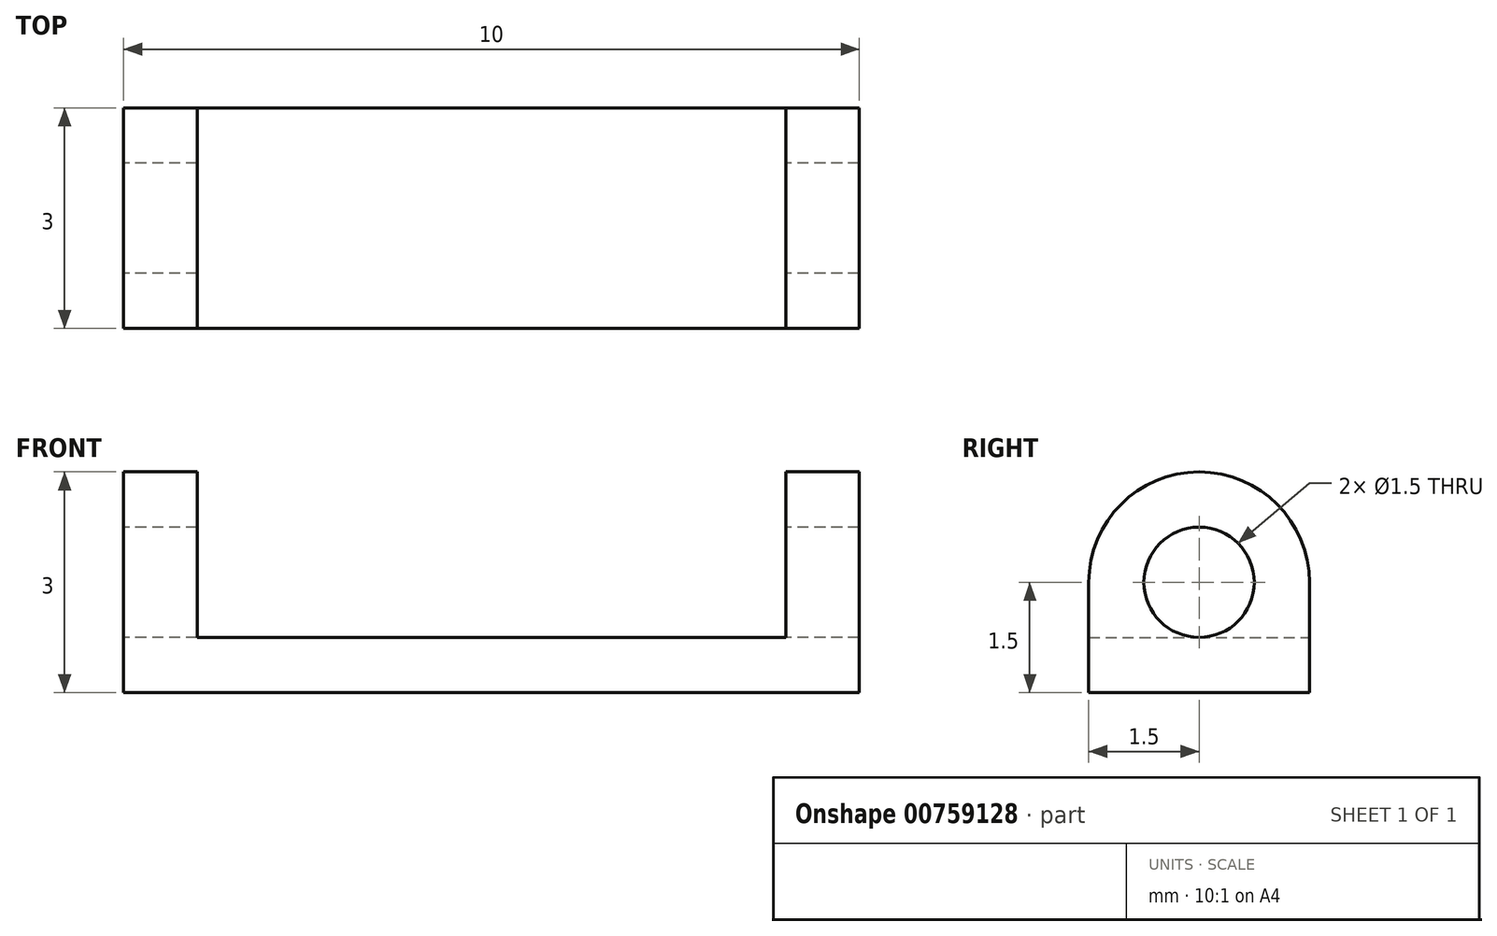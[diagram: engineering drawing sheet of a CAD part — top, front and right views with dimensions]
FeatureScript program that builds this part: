
annotation { "Feature Type Name" : "Feature", "Feature Type Description" : "" }
export const myFeature = defineFeature(function(context is Context, id is Id, definition is map)
    precondition{}
    {
        {
            assignVariable(context, id + "F0", {"name" : "b", "anyValue" : 3});
        }
        {
            var Q0;
            Q0=qCreatedBy(makeId("Top.planeOp"),FACE);
            var sketch = newSketch(context, id + "F1", { "sketchPlane" : qUnion([Q0])});
            skLineSegment(sketch, "E0.bottom", {"start": v(-5, 1.5) * mm, "end": v(5, 1.5) * mm});
            skLineSegment(sketch, "E0.top", {"start": v(-5, -1.5) * mm, "end": v(5, -1.5) * mm});
            skLineSegment(sketch, "E0.left", {"start": v(-5, 1.5) * mm, "end": v(-5, -1.5) * mm});
            skLineSegment(sketch, "E0.right", {"start": v(5, 1.5) * mm, "end": v(5, -1.5) * mm});
            skPoint(sketch, "E0.middle", {"position": v(0, 0) * mm});
            skLineSegment(sketch, "E1.bottom", {"start": v(-5, 1.5) * mm, "end": v(-4, 1.5) * mm});
            skLineSegment(sketch, "E1.top", {"start": v(-5, -1.5) * mm, "end": v(-4, -1.5) * mm});
            skLineSegment(sketch, "E1.right", {"start": v(-4, 1.5) * mm, "end": v(-4, -1.5) * mm});
            skLineSegment(sketch, "E2.bottom", {"start": v(5, 1.5) * mm, "end": v(4, 1.5) * mm});
            skLineSegment(sketch, "E2.top", {"start": v(5, -1.5) * mm, "end": v(4, -1.5) * mm});
            skLineSegment(sketch, "E2.right", {"start": v(4, 1.5) * mm, "end": v(4, -1.5) * mm});
            skSolve(sketch);
        }
        {
            var Q0;
            {var subQ0=sQuery(id+"F1.wireOp",EDGE,"E1.right");var subQ8=makeQuery(id+"F1.imprint","IMPRINT",EDGE,{"derivedFrom":subQ0});var subQ10=sQuery(id+"F1.wireOp",EDGE,"E0.left");var subQ11=sQuery(id+"F1.wireOp",EDGE,"E0.right");Q0=qUnion([makeQuery(id+"F1.imprint","IMPRINT",FACE,{"disambiguationData":[TD([[makeQuery(id+"F1.imprint","IMPRINT",EDGE,{"derivedFrom":subQ11}),-1.0]])]}),makeQuery(id+"F1.imprint","IMPRINT",FACE,{"disambiguationData":[TD([[makeQuery(id+"F1.imprint","IMPRINT",EDGE,{"derivedFrom":subQ10}),1.0]])]}),makeQuery(id+"F1.imprint","IMPRINT",FACE,{"disambiguationData":[TD([[subQ8,1.0]])]})]);}
            extrude(context, id + "F2", {"entities" : qUnion([Q0]), "depth" : 0.75 * mm, "offsetDistance" : 25 * mm});
        }
        {
            var Q0;
            {var subQ2=sQuery(id+"F1.wireOp",EDGE,"E0.left");Q0=makeQuery(id+"F1.imprint","IMPRINT",FACE,{"disambiguationData":[TD([[makeQuery(id+"F1.imprint","IMPRINT",EDGE,{"derivedFrom":subQ2}),1.0]])]});}
            var Q1;
            {var subQ0=sQuery(id+"F1.wireOp",EDGE,"E0.right");Q1=makeQuery(id+"F1.imprint","IMPRINT",FACE,{"disambiguationData":[TD([[makeQuery(id+"F1.imprint","IMPRINT",EDGE,{"derivedFrom":subQ0}),-1.0]])]});}
            extrude(context, id + "F3", {"entities" : qUnion([Q0, Q1]), "operationType" : NewBodyOperationType.ADD, "depth" : (getVariable(context, 'b')) * mm, "offsetDistance" : 25 * mm});
        }
        {
            var Q0;
            {var subQ0=sQuery(id+"F1.wireOp",EDGE,"E0.left");Q0=makeQuery(id+"F3.boolean.opBoolean","MERGE",FACE,{"derivedFrom":[makeQuery(id+"F2.opExtrude","SWEPT_FACE",FACE,{"disambiguationData":[OSD([subQ0])]}),makeQuery(id+"F3.opExtrude","SWEPT_FACE",FACE,{"disambiguationData":[OSD([subQ0])]})]});}
            var sketch = newSketch(context, id + "F4", { "sketchPlane" : qUnion([Q0])});
            skLineSegment(sketch, "E3", {"start": v(-1.5, 3) * mm, "end": v(1.5, 0) * mm, "construction": true});
            skPoint(sketch, "E4", {"position": v(0, 1.5) * mm});
            skCircle(sketch, "E5", {"center": v(0, 1.5) * mm, "radius": 0.75 * mm});
            skSolve(sketch);
        }
        {
            var Q0;
            Q0 = qSketchRegion(id + "F4", true);
            var Q1;
            Q1=makeQuery(id+"F4.imprint","IMPRINT",FACE,{"disambiguationData":[TD([[makeQuery(id+"F4.imprint","IMPRINT",EDGE,{"derivedFrom":sQuery(id+"F4.wireOp",EDGE,"E5")}),1.0]])]});
            var Q2;
            {var subQ0=sQuery(id+"F1.wireOp",EDGE,"E0.right");Q2=makeQuery(id+"F3.boolean.opBoolean","MERGE",FACE,{"derivedFrom":[makeQuery(id+"F2.opExtrude","SWEPT_FACE",FACE,{"disambiguationData":[OSD([subQ0])]}),makeQuery(id+"F3.opExtrude","SWEPT_FACE",FACE,{"disambiguationData":[OSD([subQ0])]})]});}
            extrude(context, id + "F5", {"entities" : qUnion([Q0, Q1]), "operationType" : NewBodyOperationType.REMOVE, "endBound" : BoundingType.UP_TO_SURFACE, "oppositeDirection" : true, "depth" : 25 * mm, "endBoundEntityFace" : qUnion([Q2]), "offsetDistance" : 25 * mm});
        }
        {
            var Q0;
            {var subQ0=sQuery(id+"F1.wireOp",EDGE,"E0.bottom");Q0=makeQuery(id+"F3.opExtrude","CAP_EDGE",EDGE,{"disambiguationData":[OSD([subQ0]),TDD([makeQuery(id+"F1.imprint","IMPRINT",EDGE,{"disambiguationData":[TD([[makeQuery(id+"F1.imprint","INTERSECT",VERTEX,{"derivedFrom":[subQ0,sQuery(id+"F1.wireOp",EDGE,"E0.right")]}),1.0]])],"derivedFrom":subQ0})])],"isStart":false});}
            var Q1;
            {var subQ0=sQuery(id+"F1.wireOp",EDGE,"E0.top");Q1=makeQuery(id+"F3.opExtrude","CAP_EDGE",EDGE,{"disambiguationData":[OSD([subQ0]),TDD([makeQuery(id+"F1.imprint","IMPRINT",EDGE,{"disambiguationData":[TD([[makeQuery(id+"F1.imprint","INTERSECT",VERTEX,{"derivedFrom":[subQ0,sQuery(id+"F1.wireOp",EDGE,"E0.right")]}),1.0]])],"derivedFrom":subQ0})])],"isStart":false});}
            var Q2;
            {var subQ0=sQuery(id+"F1.wireOp",EDGE,"E0.top");Q2=makeQuery(id+"F3.opExtrude","CAP_EDGE",EDGE,{"disambiguationData":[OSD([subQ0]),TDD([makeQuery(id+"F1.imprint","IMPRINT",EDGE,{"disambiguationData":[TD([[makeQuery(id+"F1.imprint","INTERSECT",VERTEX,{"derivedFrom":[subQ0,sQuery(id+"F1.wireOp",EDGE,"E1.right")]}),1.0]])],"derivedFrom":subQ0})])],"isStart":false});}
            var Q3;
            {var subQ0=sQuery(id+"F1.wireOp",EDGE,"E0.bottom");Q3=makeQuery(id+"F3.opExtrude","CAP_EDGE",EDGE,{"disambiguationData":[OSD([subQ0]),TDD([makeQuery(id+"F1.imprint","IMPRINT",EDGE,{"disambiguationData":[TD([[makeQuery(id+"F1.imprint","INTERSECT",VERTEX,{"derivedFrom":[subQ0,sQuery(id+"F1.wireOp",EDGE,"E1.right")]}),1.0]])],"derivedFrom":subQ0})])],"isStart":false});}
            fillet(context, id + "F6", {"entities" : qUnion([Q0, Q1, Q2, Q3]), "radius" : (1 / 2 * getVariable(context, 'b')) * mm, "tangentPropagation" : true, "allowEdgeOverflow" : false});
        }
    });
